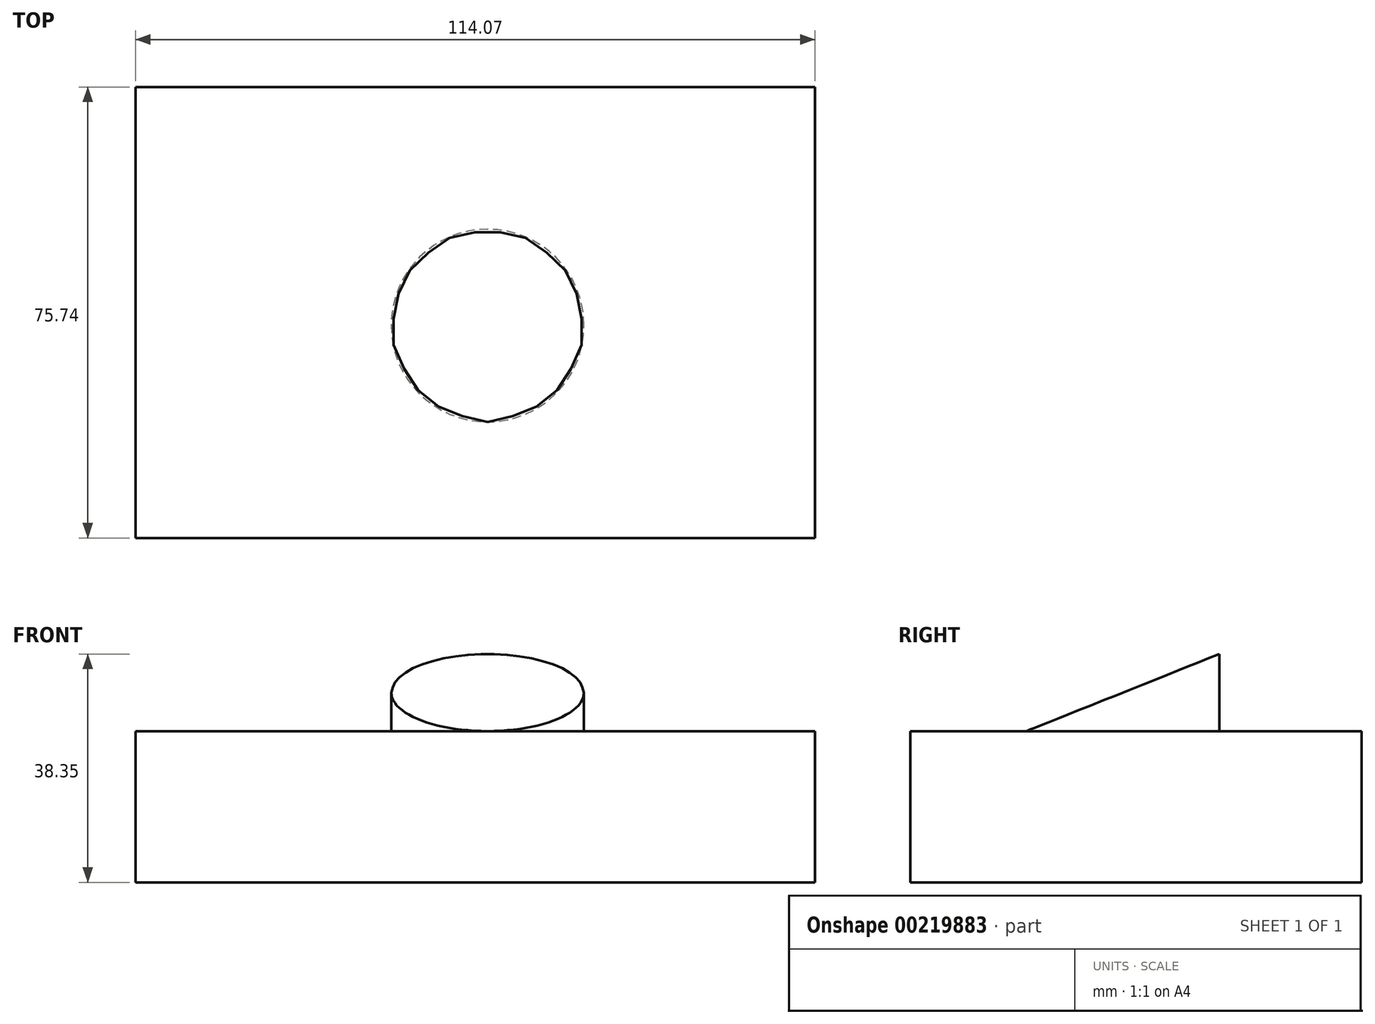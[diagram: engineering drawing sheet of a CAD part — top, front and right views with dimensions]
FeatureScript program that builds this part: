
annotation { "Feature Type Name" : "Feature", "Feature Type Description" : "" }
export const myFeature = defineFeature(function(context is Context, id is Id, definition is map)
    precondition{}
    {
        {
            var Q0;
            Q0=qCreatedBy(makeId("Front.planeOp"),FACE);
            var sketch = newSketch(context, id + "F0", { "sketchPlane" : qUnion([Q0])});
            skSolve(sketch);
        }
        {
            var Q0;
            Q0=qCreatedBy(makeId("Top.planeOp"),FACE);
            var sketch = newSketch(context, id + "F1", { "sketchPlane" : qUnion([Q0])});
            skLineSegment(sketch, "E0.bottom", {"start": v(-59.11, 40.06) * mm, "end": v(54.96, 40.06) * mm});
            skLineSegment(sketch, "E0.top", {"start": v(-59.11, -35.68) * mm, "end": v(54.96, -35.68) * mm});
            skLineSegment(sketch, "E0.left", {"start": v(-59.11, 40.06) * mm, "end": v(-59.11, -35.68) * mm});
            skLineSegment(sketch, "E0.right", {"start": v(54.96, 40.06) * mm, "end": v(54.96, -35.68) * mm});
            skSolve(sketch);
        }
        {
            var Q0;
            Q0 = qSketchRegion(id + "F0", true);
            var Q1;
            Q1 = qSketchRegion(id + "F1", true);
            extrude(context, id + "F2", {"entities" : qUnion([Q0, Q1]), "depth" : 25.4 * mm});
        }
        {
            var Q0;
            Q0=makeQuery(id+"F2.opExtrude","CAP_FACE",FACE,{"disambiguationData":[OSD([sQuery(id+"F1.wireOp",EDGE,"E0.bottom"),sQuery(id+"F1.wireOp",EDGE,"E0.top"),sQuery(id+"F1.wireOp",EDGE,"E0.left"),sQuery(id+"F1.wireOp",EDGE,"E0.right")])],"isStart":false});
            var sketch = newSketch(context, id + "F3", { "sketchPlane" : qUnion([Q0])});
            skCircle(sketch, "E1", {"center": v(0, 0) * mm, "radius": 16.18 * mm});
            skSolve(sketch);
        }
        {
            var Q0;
            Q0=makeQuery(id+"F3.imprint","IMPRINT",FACE,{"disambiguationData":[TD([[makeQuery(id+"F3.imprint","IMPRINT",EDGE,{"derivedFrom":sQuery(id+"F3.wireOp",EDGE,"E1")}),1.0]])]});
            extrude(context, id + "F4", {"entities" : qUnion([Q0]), "operationType" : NewBodyOperationType.ADD, "depth" : 12.95 * mm});
        }
        {
            var Q0;
            Q0=makeQuery(id+"F2.opExtrude","SWEPT_FACE",FACE,{"disambiguationData":[OSD([sQuery(id+"F1.wireOp",EDGE,"E0.left")])]});
            var sketch = newSketch(context, id + "F5", { "sketchPlane" : qUnion([Q0])});
            skLineSegment(sketch, "E2.0", {"start": v(-16.18, 38.35) * mm, "end": v(16.18, 38.35) * mm});
            skLineSegment(sketch, "E3", {"start": v(16.18, 38.35) * mm, "end": v(16.18, 25.4) * mm});
            skLineSegment(sketch, "E4", {"start": v(-16.18, 38.35) * mm, "end": v(16.18, 25.4) * mm});
            skSolve(sketch);
        }
        {
            var Q0;
            Q0 = qSketchRegion(id + "F5", true);
            extrude(context, id + "F6", {"entities" : qUnion([Q0]), "operationType" : NewBodyOperationType.REMOVE, "endBound" : BoundingType.THROUGH_ALL, "oppositeDirection" : true, "depth" : 25.4 * mm});
        }
    });
